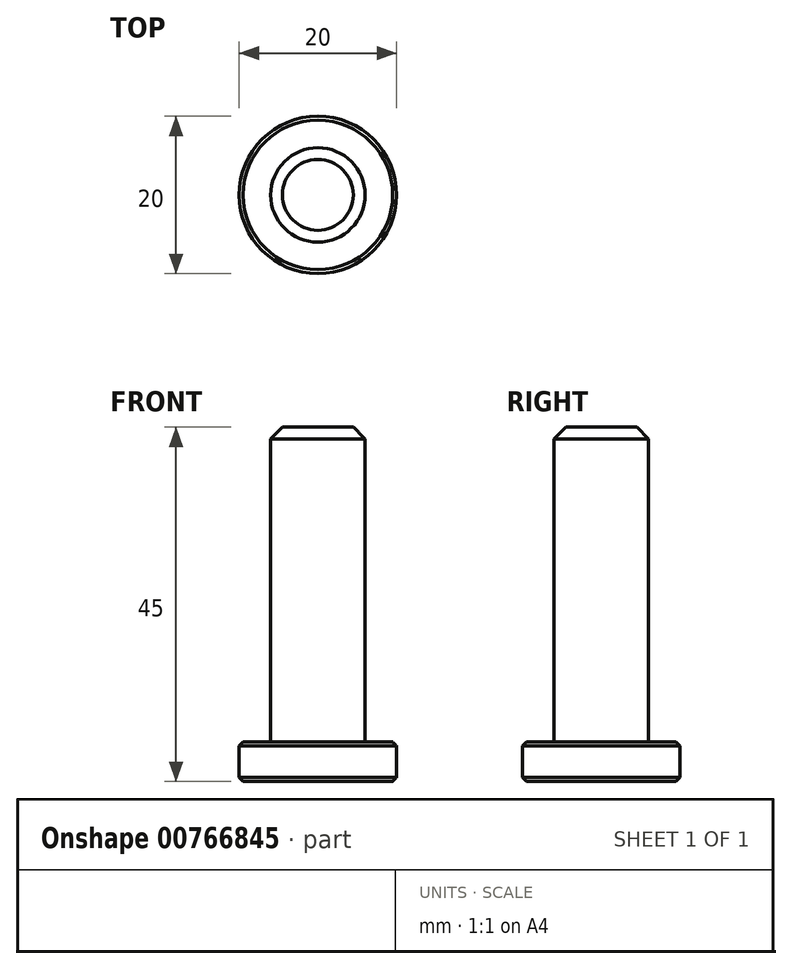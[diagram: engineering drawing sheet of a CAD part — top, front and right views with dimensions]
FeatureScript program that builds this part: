
annotation { "Feature Type Name" : "Feature", "Feature Type Description" : "" }
export const myFeature = defineFeature(function(context is Context, id is Id, definition is map)
    precondition{}
    {
        {
            var Q0;
            Q0=qCreatedBy(makeId("Top.planeOp"),FACE);
            var sketch = newSketch(context, id + "F0", { "sketchPlane" : qUnion([Q0])});
            skCircle(sketch, "E0", {"center": v(0, 0) * mm, "radius": 10 * mm});
            skPoint(sketch, "E1", {"position": v(10, 0) * mm});
            skPoint(sketch, "E2", {"position": v(-10, 0) * mm});
            skSolve(sketch);
        }
        {
            var Q0;
            Q0=makeQuery(id+"F0.imprint","IMPRINT",FACE,{"disambiguationData":[TD([[makeQuery(id+"F0.imprint","IMPRINT",EDGE,{"derivedFrom":sQuery(id+"F0.wireOp",EDGE,"E0")}),1.0]])]});
            var sketch = newSketch(context, id + "F1", { "sketchPlane" : qUnion([Q0])});
            skCircle(sketch, "E3", {"center": v(0, 0) * mm, "radius": 6 * mm});
            skPoint(sketch, "E4", {"position": v(-6, 0) * mm});
            skPoint(sketch, "E5", {"position": v(6, 0) * mm});
            skSolve(sketch);
        }
        {
            var Q0;
            Q0=makeQuery(id+"F1.imprint","IMPRINT",FACE,{"disambiguationData":[TD([[makeQuery(id+"F1.imprint","IMPRINT",EDGE,{"derivedFrom":sQuery(id+"F1.wireOp",EDGE,"E3")}),1.0]])]});
            extrude(context, id + "F2", {"entities" : qUnion([Q0]), "depth" : 40 * mm, "offsetDistance" : 25 * mm});
        }
        {
            var Q0;
            Q0=makeQuery(id+"F0.imprint","IMPRINT",FACE,{"disambiguationData":[TD([[makeQuery(id+"F0.imprint","IMPRINT",EDGE,{"derivedFrom":sQuery(id+"F0.wireOp",EDGE,"E0")}),1.0]])]});
            extrude(context, id + "F3", {"entities" : qUnion([Q0]), "operationType" : NewBodyOperationType.ADD, "oppositeDirection" : true, "depth" : 5 * mm, "offsetDistance" : 25 * mm});
        }
        {
            var Q0;
            Q0=makeQuery(id+"F3.opExtrude","CAP_EDGE",EDGE,{"disambiguationData":[OSD([sQuery(id+"F0.wireOp",EDGE,"E0")])],"isStart":true});
            var Q1;
            Q1=makeQuery(id+"F3.opExtrude","CAP_EDGE",EDGE,{"disambiguationData":[OSD([sQuery(id+"F0.wireOp",EDGE,"E0")])],"isStart":false});
            chamfer(context, id + "F4", {"entities" : qUnion([Q0, Q1]), "width" : 0.5 * mm, "tangentPropagation" : true});
        }
        {
            var Q0;
            Q0=makeQuery(id+"F2.opExtrude","CAP_EDGE",EDGE,{"disambiguationData":[OSD([sQuery(id+"F1.wireOp",EDGE,"E3")])],"isStart":false});
            chamfer(context, id + "F5", {"entities" : qUnion([Q0]), "width" : 1.5 * mm, "tangentPropagation" : true});
        }
        {
            var Q0;
            Q0=sQuery(id+"F1.wireOp",EDGE,"E3");
            extrude(context, id + "F6", {"bodyType" : ToolBodyType.SURFACE, "surfaceEntities" : qUnion([Q0]), "depth" : 5 * mm, "offsetDistance" : 25 * mm});
        }
    });
